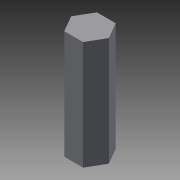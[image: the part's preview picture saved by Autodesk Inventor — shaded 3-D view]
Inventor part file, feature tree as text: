
AUTODESK INVENTOR PART (.ipt)
format: ipt  version: 2013 (Build 170138000, 138)  size: 68,096 bytes
history: native  units: in
note: dims shown in document units (in); Inventor stores cm internally (conversion verified against a paired STEP export)
features: extrude x1, sketch x1
ambient origin geometry x8: Origin, YZ Plane, XZ Plane, XY Plane, X Axis, Y Axis, Z Axis, Center Point
bodies: Solid1 (feature_tree)
feature tree (2):
  extrude  "Extrusion1"  Depth=1.25in TaperAngle=0.0deg
  sketch  "Sketch1"  dims[d0=0.375in d1=1.25in d2=0.0in]
